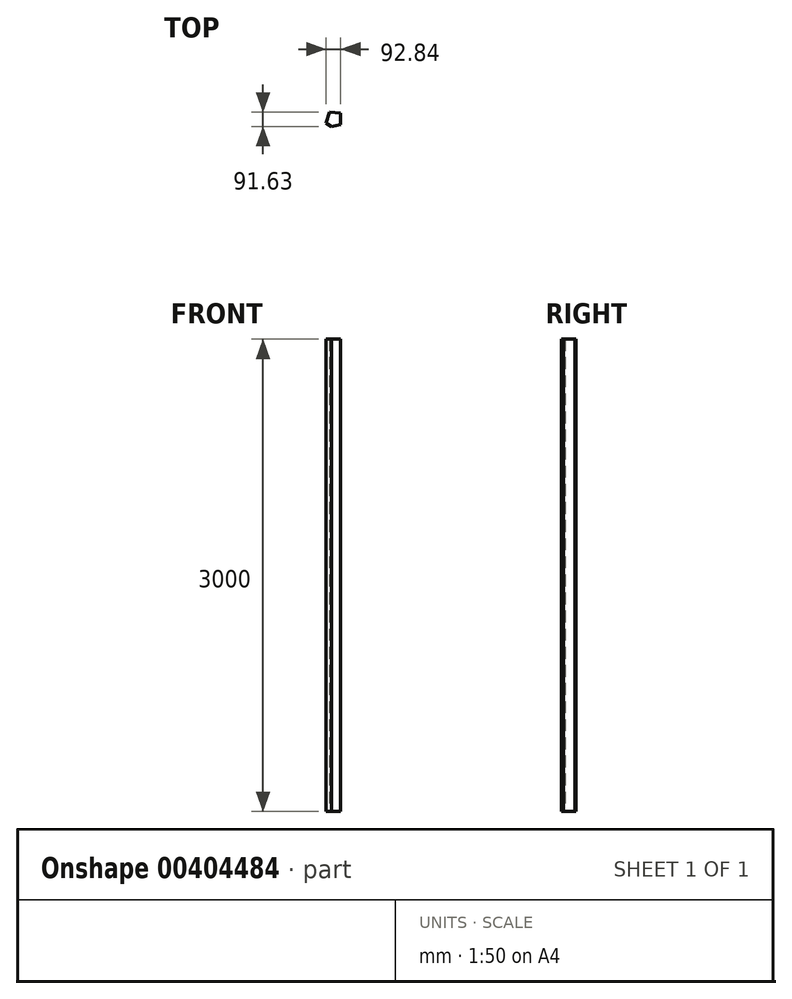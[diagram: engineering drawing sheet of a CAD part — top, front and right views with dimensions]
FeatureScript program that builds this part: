
annotation { "Feature Type Name" : "Feature", "Feature Type Description" : "" }
export const myFeature = defineFeature(function(context is Context, id is Id, definition is map)
    precondition{}
    {
        {
            var Q0;
            Q0=qCreatedBy(makeId("Top.planeOp"),FACE);
            var sketch = newSketch(context, id + "F0", { "sketchPlane" : qUnion([Q0])});
            skLineSegment(sketch, "E0", {"start": v(-38.4, 43.8) * mm, "end": v(32.4, 38.1) * mm});
            skLineSegment(sketch, "E1", {"start": v(32.4, 38.1) * mm, "end": v(31.5, -34.8) * mm});
            skLineSegment(sketch, "E2", {"start": v(31.5, -34.8) * mm, "end": v(-25.2, -47.84) * mm});
            skLineSegment(sketch, "E3", {"start": v(-25.2, -47.84) * mm, "end": v(-60.44, -26.1) * mm});
            skLineSegment(sketch, "E4", {"start": v(-60.44, -26.1) * mm, "end": v(-38.4, 43.8) * mm});
            skSolve(sketch);
        }
        {
            var Q0;
            Q0 = qSketchRegion(id + "F0", true);
            extrude(context, id + "F1", {"entities" : qUnion([Q0]), "endBound" : BoundingType.SYMMETRIC, "depth" : 3000 * mm});
        }
    });
